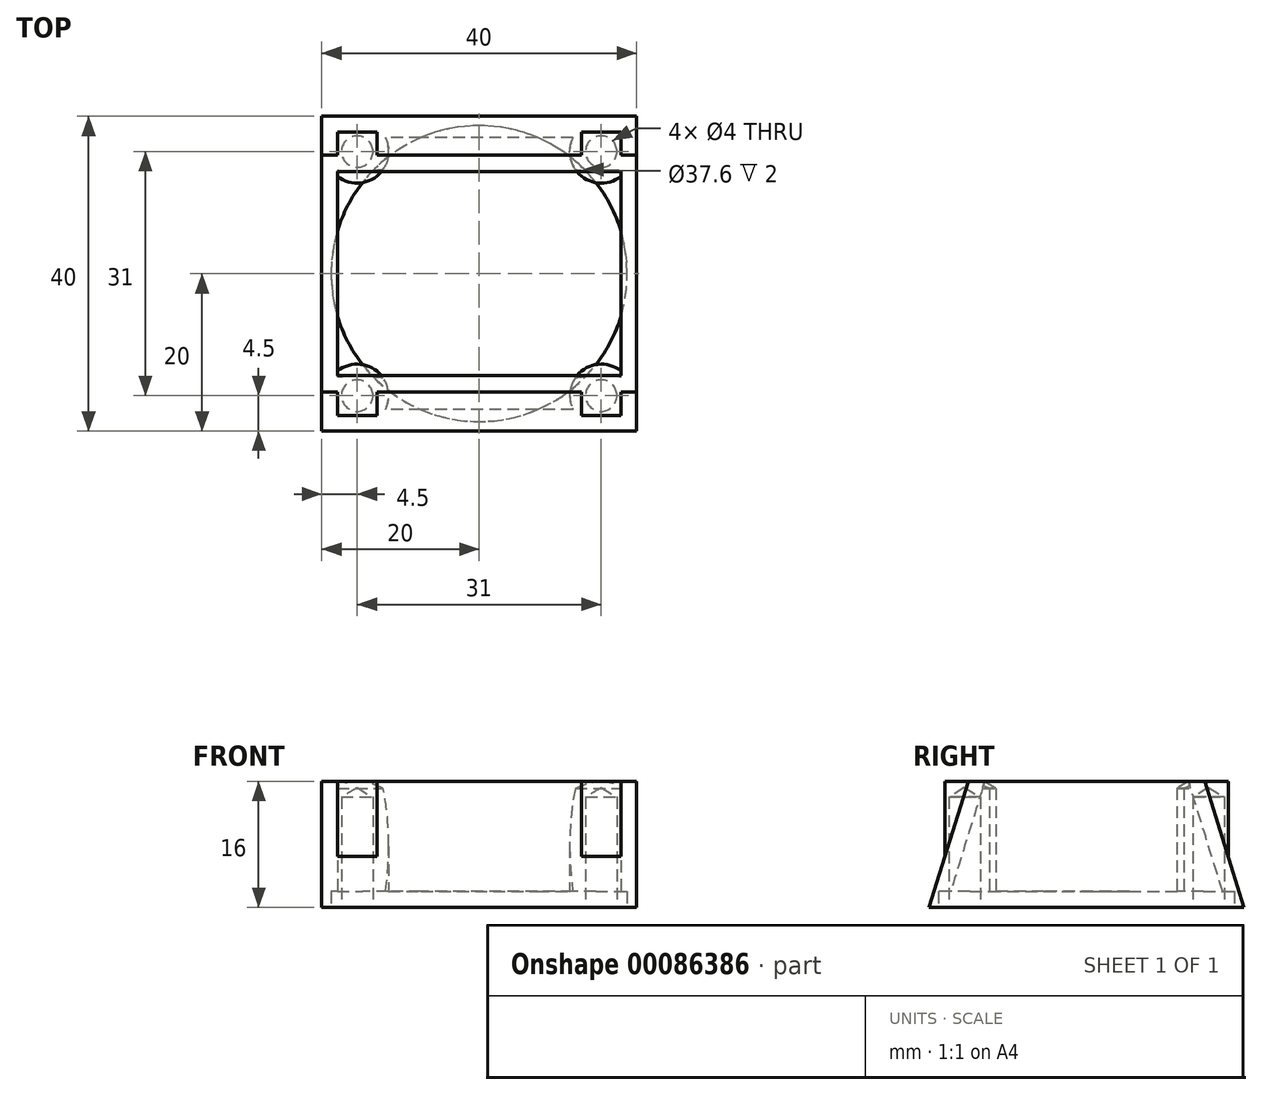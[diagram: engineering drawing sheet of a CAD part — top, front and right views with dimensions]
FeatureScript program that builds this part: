
annotation { "Feature Type Name" : "Feature", "Feature Type Description" : "" }
export const myFeature = defineFeature(function(context is Context, id is Id, definition is map)
    precondition{}
    {
        {
            var Q0;
            Q0=qCreatedBy(makeId("Right.planeOp"),FACE);
            var sketch = newSketch(context, id + "F0", { "sketchPlane" : qUnion([Q0])});
            skLineSegment(sketch, "E0", {"start": v(-20, 0) * mm, "end": v(0, 0) * mm});
            skLineSegment(sketch, "E1", {"start": v(20, 0) * mm, "end": v(4.5, 50) * mm});
            skLineSegment(sketch, "E2", {"start": v(-20, 0) * mm, "end": v(-4.5, 50) * mm});
            skLineSegment(sketch, "E3", {"start": v(0, 0) * mm, "end": v(20, 0) * mm});
            skLineSegment(sketch, "E4", {"start": v(0, 50) * mm, "end": v(0, 0) * mm, "construction": true});
            skLineSegment(sketch, "E5", {"start": v(-4.5, 50) * mm, "end": v(4.5, 50) * mm});
            skPoint(sketch, "E6", {"position": v(0, 50) * mm});
            skSolve(sketch);
        }
        {
            var Q0;
            Q0=makeQuery(id+"F0.imprint","IMPRINT",FACE,{"disambiguationData":[TD([[makeQuery(id+"F0.imprint","IMPRINT",EDGE,{"derivedFrom":sQuery(id+"F0.wireOp",EDGE,"E0")}),1.0]])]});
            extrude(context, id + "F1", {"entities" : qUnion([Q0]), "depth" : 40 * mm});
        }
        {
            var Q0;
            Q0=makeQuery(id+"F1.opExtrude","SWEPT_FACE",FACE,{"disambiguationData":[OSD([sQuery(id+"F0.wireOp",EDGE,"E0"),sQuery(id+"F0.wireOp",EDGE,"E3")])]});
            var sketch = newSketch(context, id + "F2", { "sketchPlane" : qUnion([Q0])});
            skPoint(sketch, "E7", {"position": v(20, 0) * mm});
            skPoint(sketch, "E7.positionSnap0", {"position": v(20, 20) * mm});
            skLineSegment(sketch, "E8.bottom", {"start": v(35.5, 15.5) * mm, "end": v(4.5, 15.5) * mm});
            skLineSegment(sketch, "E8.top", {"start": v(35.5, -15.5) * mm, "end": v(4.5, -15.5) * mm});
            skLineSegment(sketch, "E8.left", {"start": v(35.5, 15.5) * mm, "end": v(35.5, -15.5) * mm});
            skLineSegment(sketch, "E8.right", {"start": v(4.5, 15.5) * mm, "end": v(4.5, -15.5) * mm});
            skCircle(sketch, "E9", {"center": v(20, 0) * mm, "radius": 18.8 * mm});
            skLineSegment(sketch, "E10.bottom", {"start": v(7, 18) * mm, "end": v(2, 18) * mm});
            skLineSegment(sketch, "E10.top", {"start": v(7, 13) * mm, "end": v(2, 13) * mm});
            skLineSegment(sketch, "E10.left", {"start": v(7, 18) * mm, "end": v(7, 13) * mm});
            skLineSegment(sketch, "E10.right", {"start": v(2, 18) * mm, "end": v(2, 13) * mm});
            skPoint(sketch, "E10.middle", {"position": v(4.5, 15.5) * mm});
            skLineSegment(sketch, "E11.bottom", {"start": v(38, 18) * mm, "end": v(33, 18) * mm});
            skLineSegment(sketch, "E11.top", {"start": v(38, 13) * mm, "end": v(33, 13) * mm});
            skLineSegment(sketch, "E11.left", {"start": v(38, 18) * mm, "end": v(38, 13) * mm});
            skLineSegment(sketch, "E11.right", {"start": v(33, 18) * mm, "end": v(33, 13) * mm});
            skPoint(sketch, "E11.middle", {"position": v(35.5, 15.5) * mm});
            skLineSegment(sketch, "E12.bottom", {"start": v(2, -13) * mm, "end": v(7, -13) * mm});
            skLineSegment(sketch, "E12.top", {"start": v(2, -18) * mm, "end": v(7, -18) * mm});
            skLineSegment(sketch, "E12.left", {"start": v(2, -13) * mm, "end": v(2, -18) * mm});
            skLineSegment(sketch, "E12.right", {"start": v(7, -13) * mm, "end": v(7, -18) * mm});
            skPoint(sketch, "E12.middle", {"position": v(4.5, -15.5) * mm});
            skLineSegment(sketch, "E13.bottom", {"start": v(38, -13) * mm, "end": v(33, -13) * mm});
            skLineSegment(sketch, "E13.top", {"start": v(38, -18) * mm, "end": v(33, -18) * mm});
            skLineSegment(sketch, "E13.left", {"start": v(38, -13) * mm, "end": v(38, -18) * mm});
            skLineSegment(sketch, "E13.right", {"start": v(33, -13) * mm, "end": v(33, -18) * mm});
            skPoint(sketch, "E13.middle", {"position": v(35.5, -15.5) * mm});
            skSolve(sketch);
        }
        {
            var Q0;
            {var subQ4=sQuery(id+"F2.wireOp",EDGE,"E10.bottom");Q0=makeQuery(id+"F2.imprint","IMPRINT",FACE,{"disambiguationData":[TD([[makeQuery(id+"F2.imprint","IMPRINT",EDGE,{"derivedFrom":subQ4}),1.0]])]});}
            var Q1;
            {var subQ1=sQuery(id+"F2.wireOp",EDGE,"E8.right");var subQ5=sQuery(id+"F2.wireOp",EDGE,"E8.bottom");var subQ6=makeQuery(id+"F2.imprint","INTERSECT",VERTEX,{"derivedFrom":[subQ5,subQ1]});Q1=makeQuery(id+"F2.imprint","IMPRINT",FACE,{"disambiguationData":[TD([[makeQuery(id+"F2.imprint","IMPRINT",EDGE,{"disambiguationData":[TD([[subQ6,1.0]])],"derivedFrom":subQ5}),1.0]])]});}
            var Q2;
            {var subQ1=sQuery(id+"F2.wireOp",EDGE,"E8.left");var subQ7=sQuery(id+"F2.wireOp",EDGE,"E8.bottom");var subQ8=makeQuery(id+"F2.imprint","INTERSECT",VERTEX,{"derivedFrom":[subQ7,subQ1]});Q2=makeQuery(id+"F2.imprint","IMPRINT",FACE,{"disambiguationData":[TD([[makeQuery(id+"F2.imprint","IMPRINT",EDGE,{"disambiguationData":[TD([[subQ8,-1.0]])],"derivedFrom":subQ7}),1.0]])]});}
            var Q3;
            {var subQ4=sQuery(id+"F2.wireOp",EDGE,"E11.bottom");Q3=makeQuery(id+"F2.imprint","IMPRINT",FACE,{"disambiguationData":[TD([[makeQuery(id+"F2.imprint","IMPRINT",EDGE,{"derivedFrom":subQ4}),1.0]])]});}
            var Q4;
            {var subQ1=sQuery(id+"F2.wireOp",EDGE,"E8.left");var subQ7=sQuery(id+"F2.wireOp",EDGE,"E8.top");var subQ8=makeQuery(id+"F2.imprint","INTERSECT",VERTEX,{"derivedFrom":[subQ7,subQ1]});Q4=makeQuery(id+"F2.imprint","IMPRINT",FACE,{"disambiguationData":[TD([[makeQuery(id+"F2.imprint","IMPRINT",EDGE,{"disambiguationData":[TD([[subQ8,-1.0]])],"derivedFrom":subQ7}),-1.0]])]});}
            var Q5;
            {var subQ0=sQuery(id+"F2.wireOp",EDGE,"E13.top");Q5=makeQuery(id+"F2.imprint","IMPRINT",FACE,{"disambiguationData":[TD([[makeQuery(id+"F2.imprint","IMPRINT",EDGE,{"derivedFrom":subQ0}),-1.0]])]});}
            var Q6;
            {var subQ0=sQuery(id+"F2.wireOp",EDGE,"E12.top");Q6=makeQuery(id+"F2.imprint","IMPRINT",FACE,{"disambiguationData":[TD([[makeQuery(id+"F2.imprint","IMPRINT",EDGE,{"derivedFrom":subQ0}),1.0]])]});}
            var Q7;
            {var subQ1=sQuery(id+"F2.wireOp",EDGE,"E8.right");var subQ7=sQuery(id+"F2.wireOp",EDGE,"E8.top");var subQ8=makeQuery(id+"F2.imprint","INTERSECT",VERTEX,{"derivedFrom":[subQ7,subQ1]});Q7=makeQuery(id+"F2.imprint","IMPRINT",FACE,{"disambiguationData":[TD([[makeQuery(id+"F2.imprint","IMPRINT",EDGE,{"disambiguationData":[TD([[subQ8,1.0]])],"derivedFrom":subQ7}),-1.0]])]});}
            extrude(context, id + "F3", {"entities" : qUnion([Q0, Q1, Q2, Q3, Q4, Q5, Q6, Q7]), "operationType" : NewBodyOperationType.ADD, "oppositeDirection" : true, "depth" : 16 * mm});
        }
        {
            var Q0;
            Q0=sQuery(id+"F2.wireOp",VERTEX,"E8.right.start");
            var Q1;
            Q1=sQuery(id+"F2.wireOp",VERTEX,"E8.left.start");
            var Q2;
            Q2=sQuery(id+"F2.wireOp",VERTEX,"E8.top.start");
            var Q3;
            Q3=sQuery(id+"F2.wireOp",VERTEX,"E8.top.end");
            var Q4;
            Q4=makeQuery(id+"F1.opExtrude","SWEPT_BODY",BODY,{"disambiguationData":[OSD([sQuery(id+"F0.wireOp",EDGE,"E0"),sQuery(id+"F0.wireOp",EDGE,"E1"),sQuery(id+"F0.wireOp",EDGE,"E2"),sQuery(id+"F0.wireOp",EDGE,"E3"),sQuery(id+"F0.wireOp",EDGE,"E5")])]});
            hole(context, id + "F4", {"style" : HoleStyle.SIMPLE, "endStyle" : HoleEndStyle.BLIND, "holeDiameter" : 4 * mm, "holeDepth" : 14 * mm, "startFromSketch" : true, "locations" : qUnion([Q0, Q1, Q2, Q3]), "scope" : qUnion([Q4])});
        }
        {
            var Q0;
            Q0=makeQuery(id+"F1.opExtrude","SWEPT_FACE",FACE,{"disambiguationData":[OSD([sQuery(id+"F0.wireOp",EDGE,"E5")])]});
            shell(context, id + "F5", {"entities" : qUnion([Q0]), "thickness" : 2 * mm});
        }
        {
            var Q0;
            {var subQ0=sQuery(id+"F2.wireOp",EDGE,"E9");var subQ1=sQuery(id+"F2.wireOp",EDGE,"E8.bottom");var subQ2=makeQuery(id+"F2.imprint","INTERSECT",VERTEX,{"disambiguationData":[OD(0.0)],"derivedFrom":[subQ1,subQ0]});Q0=makeQuery(id+"F2.imprint","IMPRINT",FACE,{"disambiguationData":[TD([[makeQuery(id+"F2.imprint","IMPRINT",EDGE,{"disambiguationData":[TD([[subQ2,-1.0]])],"derivedFrom":subQ1}),-1.0]])]});}
            var Q1;
            {var subQ0=sQuery(id+"F2.wireOp",EDGE,"E9");var subQ8=sQuery(id+"F2.wireOp",EDGE,"E8.bottom");var subQ9=makeQuery(id+"F2.imprint","INTERSECT",VERTEX,{"disambiguationData":[OD(0.0)],"derivedFrom":[subQ8,subQ0]});Q1=makeQuery(id+"F2.imprint","IMPRINT",FACE,{"disambiguationData":[TD([[makeQuery(id+"F2.imprint","IMPRINT",EDGE,{"disambiguationData":[TD([[subQ9,-1.0]])],"derivedFrom":subQ8}),1.0]])]});}
            var Q2;
            {var subQ0=sQuery(id+"F2.wireOp",EDGE,"E9");var subQ1=sQuery(id+"F2.wireOp",EDGE,"E8.right");var subQ2=makeQuery(id+"F2.imprint","INTERSECT",VERTEX,{"disambiguationData":[OD(0.0)],"derivedFrom":[subQ1,subQ0]});Q2=makeQuery(id+"F2.imprint","IMPRINT",FACE,{"disambiguationData":[TD([[makeQuery(id+"F2.imprint","IMPRINT",EDGE,{"disambiguationData":[TD([[subQ2,-1.0]])],"derivedFrom":subQ1}),-1.0]])]});}
            var Q3;
            {var subQ0=sQuery(id+"F2.wireOp",EDGE,"E9");var subQ1=sQuery(id+"F2.wireOp",EDGE,"E8.left");var subQ2=makeQuery(id+"F2.imprint","INTERSECT",VERTEX,{"disambiguationData":[OD(0.0)],"derivedFrom":[subQ1,subQ0]});Q3=makeQuery(id+"F2.imprint","IMPRINT",FACE,{"disambiguationData":[TD([[makeQuery(id+"F2.imprint","IMPRINT",EDGE,{"disambiguationData":[TD([[subQ2,-1.0]])],"derivedFrom":subQ1}),1.0]])]});}
            var Q4;
            {var subQ0=sQuery(id+"F2.wireOp",EDGE,"E12.bottom");var subQ1=sQuery(id+"F2.wireOp",EDGE,"E9");var subQ2=makeQuery(id+"F2.imprint","INTERSECT",VERTEX,{"derivedFrom":[subQ1,subQ0]});Q4=makeQuery(id+"F2.imprint","IMPRINT",FACE,{"disambiguationData":[TD([[makeQuery(id+"F2.imprint","IMPRINT",EDGE,{"disambiguationData":[TD([[subQ2,-1.0]])],"derivedFrom":subQ1}),1.0]])]});}
            var Q5;
            {var subQ0=sQuery(id+"F2.wireOp",EDGE,"E10.left");var subQ1=sQuery(id+"F2.wireOp",EDGE,"E9");var subQ2=makeQuery(id+"F2.imprint","INTERSECT",VERTEX,{"derivedFrom":[subQ1,subQ0]});Q5=makeQuery(id+"F2.imprint","IMPRINT",FACE,{"disambiguationData":[TD([[makeQuery(id+"F2.imprint","IMPRINT",EDGE,{"disambiguationData":[TD([[subQ2,-1.0]])],"derivedFrom":subQ1}),1.0]])]});}
            var Q6;
            {var subQ0=sQuery(id+"F2.wireOp",EDGE,"E11.top");var subQ1=sQuery(id+"F2.wireOp",EDGE,"E9");var subQ2=makeQuery(id+"F2.imprint","INTERSECT",VERTEX,{"derivedFrom":[subQ1,subQ0]});Q6=makeQuery(id+"F2.imprint","IMPRINT",FACE,{"disambiguationData":[TD([[makeQuery(id+"F2.imprint","IMPRINT",EDGE,{"disambiguationData":[TD([[subQ2,-1.0]])],"derivedFrom":subQ1}),1.0]])]});}
            var Q7;
            {var subQ0=sQuery(id+"F2.wireOp",EDGE,"E13.right");var subQ1=sQuery(id+"F2.wireOp",EDGE,"E9");var subQ2=makeQuery(id+"F2.imprint","INTERSECT",VERTEX,{"derivedFrom":[subQ1,subQ0]});Q7=makeQuery(id+"F2.imprint","IMPRINT",FACE,{"disambiguationData":[TD([[makeQuery(id+"F2.imprint","IMPRINT",EDGE,{"disambiguationData":[TD([[subQ2,-1.0]])],"derivedFrom":subQ1}),1.0]])]});}
            var Q8;
            {var subQ0=sQuery(id+"F2.wireOp",EDGE,"E9");var subQ1=sQuery(id+"F2.wireOp",EDGE,"E8.top");var subQ2=makeQuery(id+"F2.imprint","INTERSECT",VERTEX,{"disambiguationData":[OD(0.0)],"derivedFrom":[subQ1,subQ0]});Q8=makeQuery(id+"F2.imprint","IMPRINT",FACE,{"disambiguationData":[TD([[makeQuery(id+"F2.imprint","IMPRINT",EDGE,{"disambiguationData":[TD([[subQ2,-1.0]])],"derivedFrom":subQ1}),1.0]])]});}
            extrude(context, id + "F6", {"entities" : qUnion([Q0, Q1, Q2, Q3, Q4, Q5, Q6, Q7, Q8]), "operationType" : NewBodyOperationType.REMOVE, "oppositeDirection" : true, "depth" : 2 * mm});
        }
        {
            var Q0;
            Q0=makeQuery(id+"F1.opExtrude","CAP_FACE",FACE,{"disambiguationData":[OSD([sQuery(id+"F0.wireOp",EDGE,"E0"),sQuery(id+"F0.wireOp",EDGE,"E1"),sQuery(id+"F0.wireOp",EDGE,"E2"),sQuery(id+"F0.wireOp",EDGE,"E3"),sQuery(id+"F0.wireOp",EDGE,"E5")])],"isStart":true});
            var sketch = newSketch(context, id + "F7", { "sketchPlane" : qUnion([Q0])});
            skLineSegment(sketch, "E14.bottom", {"start": v(-20, 0) * mm, "end": v(20, 0) * mm});
            skLineSegment(sketch, "E14.top", {"start": v(-20, 16) * mm, "end": v(20, 16) * mm});
            skLineSegment(sketch, "E14.left", {"start": v(-20, 0) * mm, "end": v(-20, 16) * mm});
            skLineSegment(sketch, "E14.right", {"start": v(20, 0) * mm, "end": v(20, 16) * mm});
            skSolve(sketch);
        }
        {
            var Q0;
            {var subQ0=sQuery(id+"F7.wireOp",EDGE,"E14.bottom");Q0=makeQuery(id+"F7.imprint","IMPRINT",FACE,{"disambiguationData":[TD([[makeQuery(id+"F7.imprint","IMPRINT",EDGE,{"derivedFrom":subQ0}),-1.0]])]});}
            var Q1;
            {var subQ0=sQuery(id+"F7.wireOp",EDGE,"E14.left");Q1=makeQuery(id+"F7.imprint","IMPRINT",FACE,{"disambiguationData":[TD([[makeQuery(id+"F7.imprint","IMPRINT",EDGE,{"derivedFrom":subQ0}),-1.0]])]});}
            var Q2;
            {var subQ0=sQuery(id+"F7.wireOp",EDGE,"E14.right");Q2=makeQuery(id+"F7.imprint","IMPRINT",FACE,{"disambiguationData":[TD([[makeQuery(id+"F7.imprint","IMPRINT",EDGE,{"derivedFrom":subQ0}),1.0]])]});}
            var Q3;
            Q3=makeQuery(id+"F1.opExtrude","CAP_FACE",FACE,{"disambiguationData":[OSD([sQuery(id+"F0.wireOp",EDGE,"E0"),sQuery(id+"F0.wireOp",EDGE,"E1"),sQuery(id+"F0.wireOp",EDGE,"E2"),sQuery(id+"F0.wireOp",EDGE,"E3"),sQuery(id+"F0.wireOp",EDGE,"E5")])],"isStart":false});
            extrude(context, id + "F8", {"entities" : qUnion([Q0, Q1, Q2]), "operationType" : NewBodyOperationType.INTERSECT, "endBound" : BoundingType.UP_TO_SURFACE, "oppositeDirection" : true, "endBoundEntityFace" : qUnion([Q3]), "depth" : 40 * mm});
        }
    });
